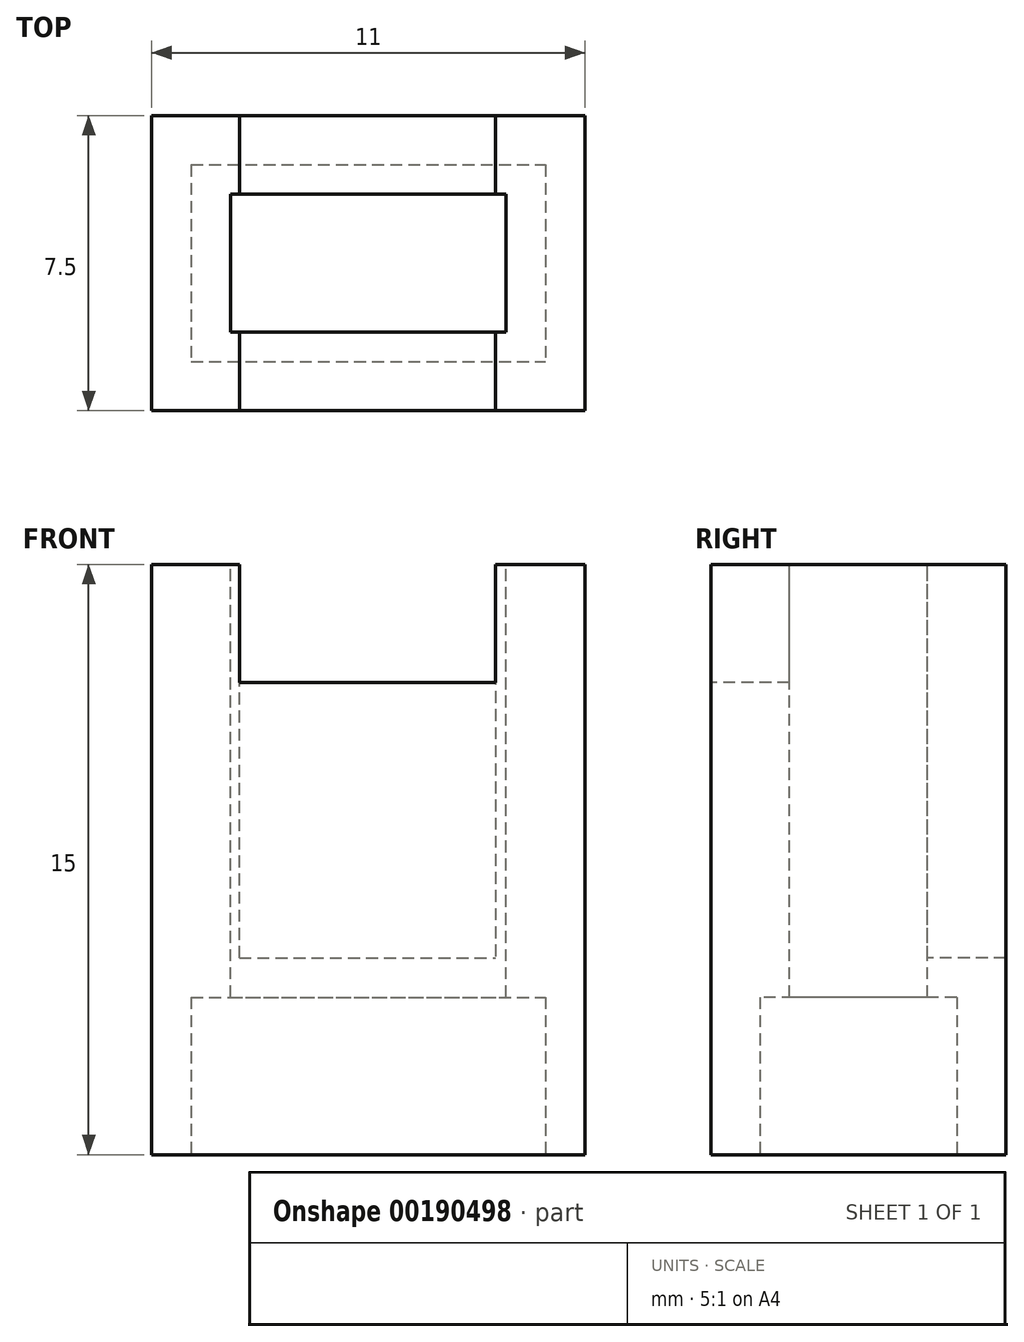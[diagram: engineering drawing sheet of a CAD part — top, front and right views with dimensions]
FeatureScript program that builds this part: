
annotation { "Feature Type Name" : "Feature", "Feature Type Description" : "" }
export const myFeature = defineFeature(function(context is Context, id is Id, definition is map)
    precondition{}
    {
        {
            var Q0;
            Q0=qCreatedBy(makeId("Right.planeOp"),FACE);
            var sketch = newSketch(context, id + "F0", { "sketchPlane" : qUnion([Q0])});
            skLineSegment(sketch, "E0.bottom", {"start": v(3.75, -7.5) * mm, "end": v(-3.75, -7.5) * mm});
            skLineSegment(sketch, "E0.top", {"start": v(3.75, 7.5) * mm, "end": v(-3.75, 7.5) * mm});
            skLineSegment(sketch, "E0.left", {"start": v(3.75, -7.5) * mm, "end": v(3.75, 7.5) * mm});
            skLineSegment(sketch, "E0.right", {"start": v(-3.75, -7.5) * mm, "end": v(-3.75, 7.5) * mm});
            skPoint(sketch, "E0.middle", {"position": v(0, 0) * mm});
            skSolve(sketch);
        }
        {
            var Q0;
            Q0=makeQuery(id+"F0.imprint","IMPRINT",FACE,{"disambiguationData":[TD([[makeQuery(id+"F0.imprint","IMPRINT",EDGE,{"derivedFrom":sQuery(id+"F0.wireOp",EDGE,"E0.bottom")}),-1.0]])]});
            extrude(context, id + "F1", {"entities" : qUnion([Q0]), "depth" : 11 * mm});
        }
        {
            var Q0;
            Q0=makeQuery(id+"F1.opExtrude","SWEPT_FACE",FACE,{"disambiguationData":[OSD([sQuery(id+"F0.wireOp",EDGE,"E0.top")])]});
            var sketch = newSketch(context, id + "F2", { "sketchPlane" : qUnion([Q0])});
            skLineSegment(sketch, "E1.bottom", {"start": v(9, -1.75) * mm, "end": v(2, -1.75) * mm});
            skLineSegment(sketch, "E1.top", {"start": v(9, 1.75) * mm, "end": v(2, 1.75) * mm});
            skLineSegment(sketch, "E1.left", {"start": v(9, -1.75) * mm, "end": v(9, 1.75) * mm});
            skLineSegment(sketch, "E1.right", {"start": v(2, -1.75) * mm, "end": v(2, 1.75) * mm});
            skPoint(sketch, "E1.middle", {"position": v(5.5, 0) * mm});
            skPoint(sketch, "E1.middle.positionSnap0", {"position": v(5.5, 3.75) * mm});
            skPoint(sketch, "E1.centerSnap0", {"position": v(5.5, 3.75) * mm});
            skSolve(sketch);
        }
        {
            var Q0;
            Q0=makeQuery(id+"F2.imprint","IMPRINT",FACE,{"disambiguationData":[TD([[makeQuery(id+"F2.imprint","IMPRINT",EDGE,{"derivedFrom":sQuery(id+"F2.wireOp",EDGE,"E1.bottom")}),-1.0]])]});
            extrude(context, id + "F3", {"entities" : qUnion([Q0]), "operationType" : NewBodyOperationType.REMOVE, "oppositeDirection" : true, "depth" : 20 * mm});
        }
        {
            var Q0;
            Q0=makeQuery(id+"F1.opExtrude","SWEPT_FACE",FACE,{"disambiguationData":[OSD([sQuery(id+"F0.wireOp",EDGE,"E0.bottom")])]});
            var sketch = newSketch(context, id + "F4", { "sketchPlane" : qUnion([Q0])});
            skLineSegment(sketch, "E2.bottom", {"start": v(1, -2.5) * mm, "end": v(10, -2.5) * mm});
            skLineSegment(sketch, "E2.top", {"start": v(1, 2.5) * mm, "end": v(10, 2.5) * mm});
            skLineSegment(sketch, "E2.left", {"start": v(1, -2.5) * mm, "end": v(1, 2.5) * mm});
            skLineSegment(sketch, "E2.right", {"start": v(10, -2.5) * mm, "end": v(10, 2.5) * mm});
            skPoint(sketch, "E2.middle", {"position": v(5.5, 0) * mm});
            skPoint(sketch, "E2.middle.positionSnap0", {"position": v(5.5, -3.75) * mm});
            skPoint(sketch, "E2.centerSnap0", {"position": v(5.5, -3.75) * mm});
            skSolve(sketch);
        }
        {
            var Q0;
            Q0=makeQuery(id+"F4.imprint","IMPRINT",FACE,{"disambiguationData":[TD([[makeQuery(id+"F4.imprint","IMPRINT",EDGE,{"derivedFrom":sQuery(id+"F4.wireOp",EDGE,"E2.bottom")}),1.0]])]});
            extrude(context, id + "F5", {"entities" : qUnion([Q0]), "operationType" : NewBodyOperationType.REMOVE, "oppositeDirection" : true, "depth" : 4 * mm});
        }
        {
            var Q0;
            Q0=makeQuery(id+"F1.opExtrude","SWEPT_FACE",FACE,{"disambiguationData":[OSD([sQuery(id+"F0.wireOp",EDGE,"E0.right")])]});
            var sketch = newSketch(context, id + "F6", { "sketchPlane" : qUnion([Q0])});
            skLineSegment(sketch, "E3", {"start": v(-3.11, 4.5) * mm, "end": v(15.3, 4.5) * mm, "construction": true});
            skLineSegment(sketch, "E4", {"start": v(2.22, 7.5) * mm, "end": v(2.22, 4.5) * mm});
            skLineSegment(sketch, "E5", {"start": v(2.22, 4.5) * mm, "end": v(8.74, 4.5) * mm});
            skLineSegment(sketch, "E6", {"start": v(8.74, 4.5) * mm, "end": v(8.74, 7.5) * mm});
            skLineSegment(sketch, "E7", {"start": v(8.74, 7.5) * mm, "end": v(2.22, 7.5) * mm});
            skSolve(sketch);
        }
        {
            var Q0;
            Q0=makeQuery(id+"F6.imprint","IMPRINT",FACE,{"disambiguationData":[TD([[makeQuery(id+"F6.imprint","IMPRINT",EDGE,{"derivedFrom":sQuery(id+"F6.wireOp",EDGE,"E4")}),1.0]])]});
            extrude(context, id + "F7", {"entities" : qUnion([Q0]), "operationType" : NewBodyOperationType.REMOVE, "oppositeDirection" : true, "depth" : 25 * mm});
        }
        {
            var Q0;
            Q0=qCreatedBy(makeId("Front.planeOp"),FACE);
            var sketch = newSketch(context, id + "F8", { "sketchPlane" : qUnion([Q0])});
            skLineSegment(sketch, "E8.0", {"start": v(2.22, 4.5) * mm, "end": v(8.74, 4.5) * mm});
            skLineSegment(sketch, "E9", {"start": v(8.74, 4.5) * mm, "end": v(8.74, -2.5) * mm});
            skLineSegment(sketch, "E10", {"start": v(8.74, -2.5) * mm, "end": v(2.22, -2.5) * mm});
            skLineSegment(sketch, "E11", {"start": v(2.22, -2.5) * mm, "end": v(2.22, 4.5) * mm});
            skSolve(sketch);
        }
        {
            var Q0;
            Q0=makeQuery(id+"F8.imprint","IMPRINT",FACE,{"disambiguationData":[TD([[makeQuery(id+"F8.imprint","IMPRINT",EDGE,{"derivedFrom":sQuery(id+"F8.wireOp",EDGE,"E8.0")}),-1.0]])]});
            extrude(context, id + "F9", {"entities" : qUnion([Q0]), "operationType" : NewBodyOperationType.REMOVE, "oppositeDirection" : true, "depth" : 25 * mm});
        }
    });
